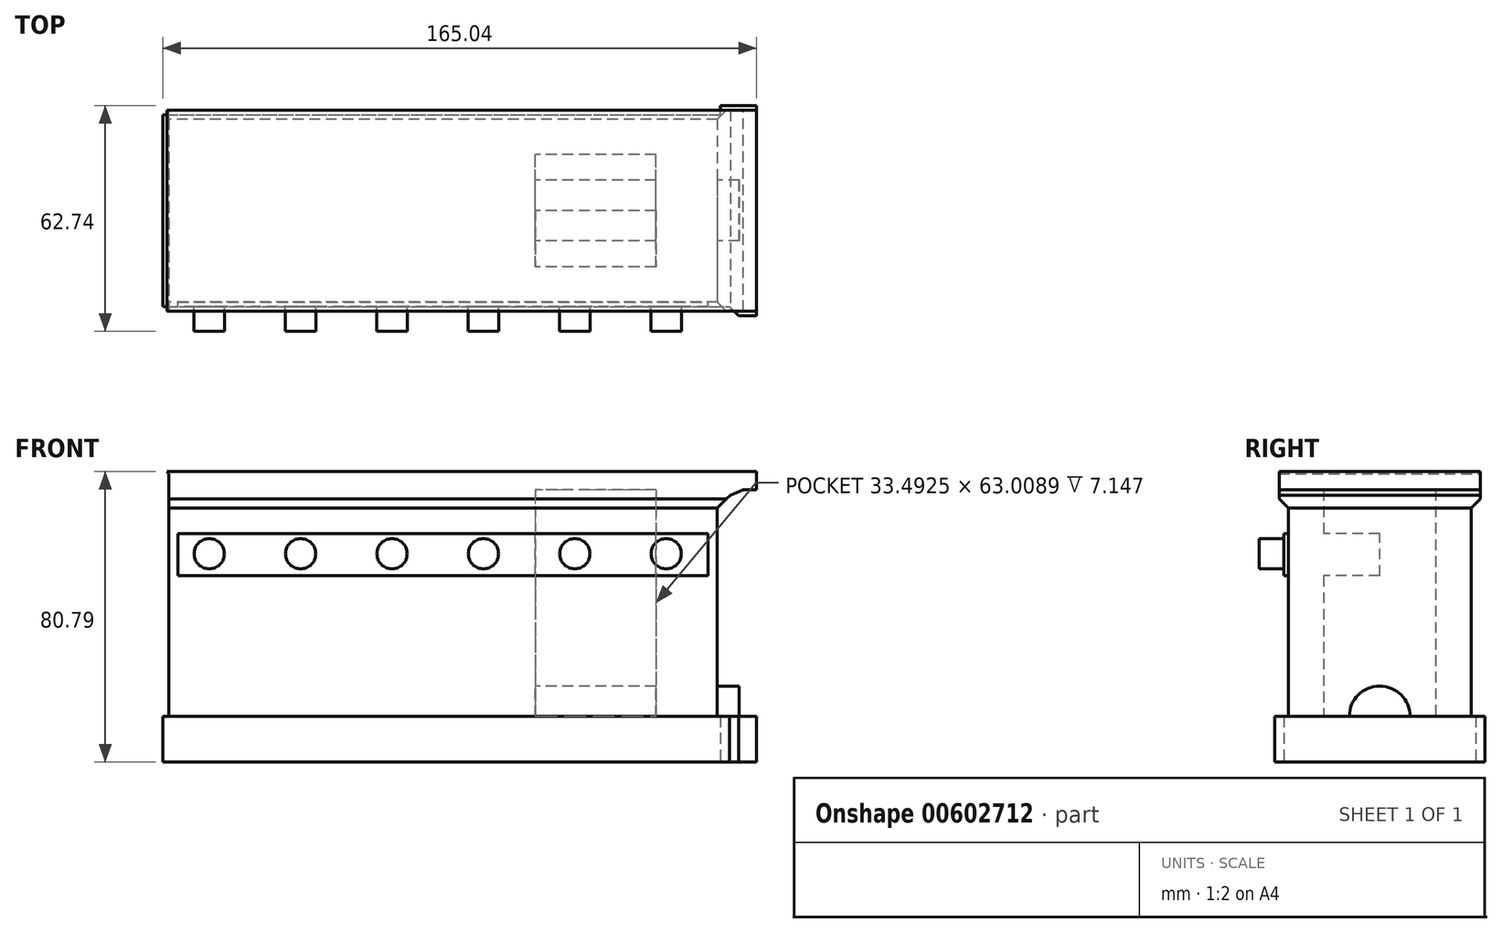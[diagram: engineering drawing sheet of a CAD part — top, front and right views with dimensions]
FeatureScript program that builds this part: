
annotation { "Feature Type Name" : "Feature", "Feature Type Description" : "" }
export const myFeature = defineFeature(function(context is Context, id is Id, definition is map)
    precondition{}
    {
        {
            var Q0;
            Q0=qCreatedBy(makeId("Top.planeOp"),FACE);
            var sketch = newSketch(context, id + "F0", { "sketchPlane" : qUnion([Q0])});
            skLineSegment(sketch, "E0.bottom", {"start": v(76.2, 25.4) * mm, "end": v(-76.2, 25.4) * mm});
            skLineSegment(sketch, "E0.top", {"start": v(76.2, -25.4) * mm, "end": v(-76.2, -25.4) * mm});
            skLineSegment(sketch, "E0.left", {"start": v(76.2, 25.4) * mm, "end": v(76.2, -25.4) * mm});
            skLineSegment(sketch, "E0.right", {"start": v(-76.2, 25.4) * mm, "end": v(-76.2, -25.4) * mm});
            skPoint(sketch, "E0.middle", {"position": v(0, 0) * mm});
            skLineSegment(sketch, "E1.bottom", {"start": v(59.13, -15.58) * mm, "end": v(25.64, -15.58) * mm});
            skLineSegment(sketch, "E1.top", {"start": v(59.13, 15.58) * mm, "end": v(25.64, 15.58) * mm});
            skLineSegment(sketch, "E1.left", {"start": v(59.13, -15.58) * mm, "end": v(59.13, 15.58) * mm});
            skLineSegment(sketch, "E1.right", {"start": v(25.64, -15.58) * mm, "end": v(25.64, 15.58) * mm});
            skPoint(sketch, "E1.middle", {"position": v(42.39, 0) * mm});
            skSolve(sketch);
        }
        {
            var Q0;
            Q0 = qSketchRegion(id + "F0", true);
            extrude(context, id + "F1", {"entities" : qUnion([Q0]), "depth" : 63.5 * mm, "offsetDistance" : 25.4 * mm});
        }
        {
            var Q0;
            Q0=qCreatedBy(makeId("Front.planeOp"),FACE);
            var sketch = newSketch(context, id + "F2", { "sketchPlane" : qUnion([Q0])});
            skLineSegment(sketch, "E2.bottom", {"start": v(-77.93, 0) * mm, "end": v(77.01, 0) * mm});
            skLineSegment(sketch, "E2.top", {"start": v(-77.93, -12.7) * mm, "end": v(77.01, -12.7) * mm});
            skLineSegment(sketch, "E2.left", {"start": v(-77.93, 0) * mm, "end": v(-77.93, -12.7) * mm});
            skLineSegment(sketch, "E2.right", {"start": v(77.01, 0) * mm, "end": v(77.01, -12.7) * mm});
            skLineSegment(sketch, "E3.bottom", {"start": v(-76.78, 63) * mm, "end": v(87.11, 63) * mm});
            skLineSegment(sketch, "E3.top", {"start": v(-76.78, 68.09) * mm, "end": v(87.11, 68.09) * mm});
            skLineSegment(sketch, "E3.left", {"start": v(-76.78, 63) * mm, "end": v(-76.78, 68.09) * mm});
            skLineSegment(sketch, "E3.right", {"start": v(87.11, 63) * mm, "end": v(87.11, 68.09) * mm});
            skLineSegment(sketch, "E4.bottom", {"start": v(77.01, 0) * mm, "end": v(87.11, 0) * mm});
            skLineSegment(sketch, "E4.top", {"start": v(77.01, -12.7) * mm, "end": v(87.11, -12.7) * mm});
            skLineSegment(sketch, "E4.right", {"start": v(87.11, 0) * mm, "end": v(87.11, -12.7) * mm});
            skLineSegment(sketch, "E5.bottom", {"start": v(65.76, -12.7) * mm, "end": v(4.48, -12.7) * mm});
            skLineSegment(sketch, "E5.top", {"start": v(65.76, -27.16) * mm, "end": v(4.48, -27.16) * mm});
            skLineSegment(sketch, "E5.left", {"start": v(65.76, -12.7) * mm, "end": v(65.76, -27.16) * mm});
            skLineSegment(sketch, "E5.right", {"start": v(4.48, -12.7) * mm, "end": v(4.48, -27.16) * mm});
            skSolve(sketch);
        }
        {
            var Q0;
            Q0=makeQuery(id+"F2.imprint","IMPRINT",FACE,{"disambiguationData":[TD([[makeQuery(id+"F2.imprint","IMPRINT",EDGE,{"derivedFrom":sQuery(id+"F2.wireOp",EDGE,"E2.bottom")}),-1.0]])]});
            extrude(context, id + "F3", {"entities" : qUnion([Q0]), "operationType" : NewBodyOperationType.ADD, "endBound" : BoundingType.SYMMETRIC, "depth" : 53.34 * mm, "offsetDistance" : 25.4 * mm});
        }
        {
            var Q0;
            Q0=makeQuery(id+"F2.imprint","IMPRINT",FACE,{"disambiguationData":[TD([[makeQuery(id+"F2.imprint","IMPRINT",EDGE,{"derivedFrom":sQuery(id+"F2.wireOp",EDGE,"E3.bottom")}),1.0]])]});
            extrude(context, id + "F4", {"entities" : qUnion([Q0]), "operationType" : NewBodyOperationType.ADD, "endBound" : BoundingType.SYMMETRIC, "depth" : 55.88 * mm, "offsetDistance" : 25.4 * mm});
        }
        {
            var Q0;
            Q0=makeQuery(id+"F2.imprint","IMPRINT",FACE,{"disambiguationData":[TD([[makeQuery(id+"F2.imprint","IMPRINT",EDGE,{"derivedFrom":sQuery(id+"F2.wireOp",EDGE,"E4.bottom")}),-1.0]])]});
            extrude(context, id + "F5", {"entities" : qUnion([Q0]), "operationType" : NewBodyOperationType.ADD, "endBound" : BoundingType.SYMMETRIC, "depth" : 58.42 * mm, "offsetDistance" : 25.4 * mm});
        }
        {
            var Q0;
            Q0=makeQuery(id+"F5.opExtrude","CAP_EDGE",EDGE,{"disambiguationData":[OSD([sQuery(id+"F2.wireOp",EDGE,"E2.right")])],"isStart":false});
            var Q1;
            Q1=makeQuery(id+"F4.boolean.opBoolean","INTERSECT",EDGE,{"derivedFrom":[makeQuery(id+"F1.opExtrude","SWEPT_FACE",FACE,{"disambiguationData":[OSD([sQuery(id+"F0.wireOp",EDGE,"E0.top")])]}),makeQuery(id+"F4.opExtrude","SWEPT_FACE",FACE,{"disambiguationData":[OSD([sQuery(id+"F2.wireOp",EDGE,"E3.bottom")])]})]});
            var Q2;
            Q2=makeQuery(id+"F4.boolean.opBoolean","INTERSECT",EDGE,{"derivedFrom":[makeQuery(id+"F1.opExtrude","SWEPT_FACE",FACE,{"disambiguationData":[OSD([sQuery(id+"F0.wireOp",EDGE,"E0.bottom")])]}),makeQuery(id+"F4.opExtrude","SWEPT_FACE",FACE,{"disambiguationData":[OSD([sQuery(id+"F2.wireOp",EDGE,"E3.bottom")])]})]});
            chamfer(context, id + "F6", {"entities" : qUnion([Q0, Q1, Q2]), "width" : 5.08 * mm, "tangentPropagation" : true});
        }
        {
            var Q0;
            Q0=makeQuery(id+"F4.opExtrude","SWEPT_EDGE",EDGE,{"disambiguationData":[OSD([sQuery(id+"F2.wireOp",EDGE,"E3.bottom"),sQuery(id+"F2.wireOp",EDGE,"E3.left")])]});
            chamfer(context, id + "F7", {"entities" : qUnion([Q0]), "width" : 5.08 * mm, "tangentPropagation" : true});
        }
        {
            var Q0;
            Q0=makeQuery(id+"F4.boolean.opBoolean","INTERSECT",EDGE,{"derivedFrom":[makeQuery(id+"F1.opExtrude","SWEPT_FACE",FACE,{"disambiguationData":[OSD([sQuery(id+"F0.wireOp",EDGE,"E0.left")])]}),makeQuery(id+"F4.opExtrude","SWEPT_FACE",FACE,{"disambiguationData":[OSD([sQuery(id+"F2.wireOp",EDGE,"E3.bottom")])]})]});
            chamfer(context, id + "F8", {"entities" : qUnion([Q0]), "width" : 5.08 * mm, "tangentPropagation" : true});
        }
        {
            var Q0;
            {var subQ0=makeQuery(id+"F4.opExtrude","SWEPT_FACE",FACE,{"disambiguationData":[OSD([sQuery(id+"F2.wireOp",EDGE,"E3.bottom")])]});Q0=makeQuery(id+"F8.opChamfer","BLEND_EDGE",EDGE,{"blendedFrom":[makeQuery(id+"F4.boolean.opBoolean","INTERSECT",EDGE,{"derivedFrom":[makeQuery(id+"F1.opExtrude","SWEPT_FACE",FACE,{"disambiguationData":[OSD([sQuery(id+"F0.wireOp",EDGE,"E0.left")])]}),subQ0]}),makeQuery(id+"F6.opChamfer","SPLIT",FACE,{"disambiguationData":[OD(1.0)],"derivedFrom":subQ0})],"blendedInto":[makeQuery(id+"F6.opChamfer","SPLIT",FACE,{"disambiguationData":[OD(1.0)],"derivedFrom":subQ0})]});}
            chamfer(context, id + "F9", {"entities" : qUnion([Q0]), "width" : 5.08 * mm, "tangentPropagation" : true});
        }
        {
            var Q0;
            Q0=qCreatedBy(makeId("Front.planeOp"),FACE);
            var sketch = newSketch(context, id + "F10", { "sketchPlane" : qUnion([Q0])});
            skCircle(sketch, "E6", {"center": v(-65.01, 45.23) * mm, "radius": 4.2 * mm});
            skCircle(sketch, "E7", {"center": v(-39.61, 45.23) * mm, "radius": 4.2 * mm});
            skCircle(sketch, "E8", {"center": v(-14.21, 45.23) * mm, "radius": 4.2 * mm});
            skCircle(sketch, "E9", {"center": v(11.19, 45.23) * mm, "radius": 4.2 * mm});
            skCircle(sketch, "E10", {"center": v(36.59, 45.23) * mm, "radius": 4.2 * mm});
            skCircle(sketch, "E11", {"center": v(61.99, 45.23) * mm, "radius": 4.2 * mm});
            skSolve(sketch);
        }
        {
            var Q0;
            Q0 = qSketchRegion(id + "F10", true);
            extrude(context, id + "F11", {"entities" : qUnion([Q0]), "operationType" : NewBodyOperationType.ADD, "depth" : 33.53 * mm, "offsetDistance" : 25.4 * mm});
        }
        {
            var Q0;
            Q0=qCreatedBy(makeId("Front.planeOp"),FACE);
            var sketch = newSketch(context, id + "F12", { "sketchPlane" : qUnion([Q0])});
            skLineSegment(sketch, "E12.bottom", {"start": v(73.66, 50.83) * mm, "end": v(-73.66, 50.83) * mm});
            skLineSegment(sketch, "E12.top", {"start": v(73.66, 39.08) * mm, "end": v(-73.66, 39.08) * mm});
            skLineSegment(sketch, "E12.left", {"start": v(73.66, 50.83) * mm, "end": v(73.66, 39.08) * mm});
            skLineSegment(sketch, "E12.right", {"start": v(-73.66, 50.83) * mm, "end": v(-73.66, 39.08) * mm});
            skPoint(sketch, "E12.middle", {"position": v(0, 44.96) * mm});
            skSolve(sketch);
        }
        {
            var Q0;
            Q0 = qSketchRegion(id + "F12", true);
            extrude(context, id + "F13", {"entities" : qUnion([Q0]), "operationType" : NewBodyOperationType.ADD, "depth" : 26.67 * mm, "offsetDistance" : 25.4 * mm});
        }
        {
            var Q0;
            Q0=qCreatedBy(makeId("Right.planeOp"),FACE);
            var sketch = newSketch(context, id + "F14", { "sketchPlane" : qUnion([Q0])});
            skCircle(sketch, "E13", {"center": v(0, 0) * mm, "radius": 8.44 * mm});
            skSolve(sketch);
        }
        {
            var Q0;
            Q0 = qSketchRegion(id + "F14", true);
            extrude(context, id + "F15", {"entities" : qUnion([Q0]), "operationType" : NewBodyOperationType.ADD, "depth" : 82.3 * mm, "offsetDistance" : 25.4 * mm});
        }
    });
